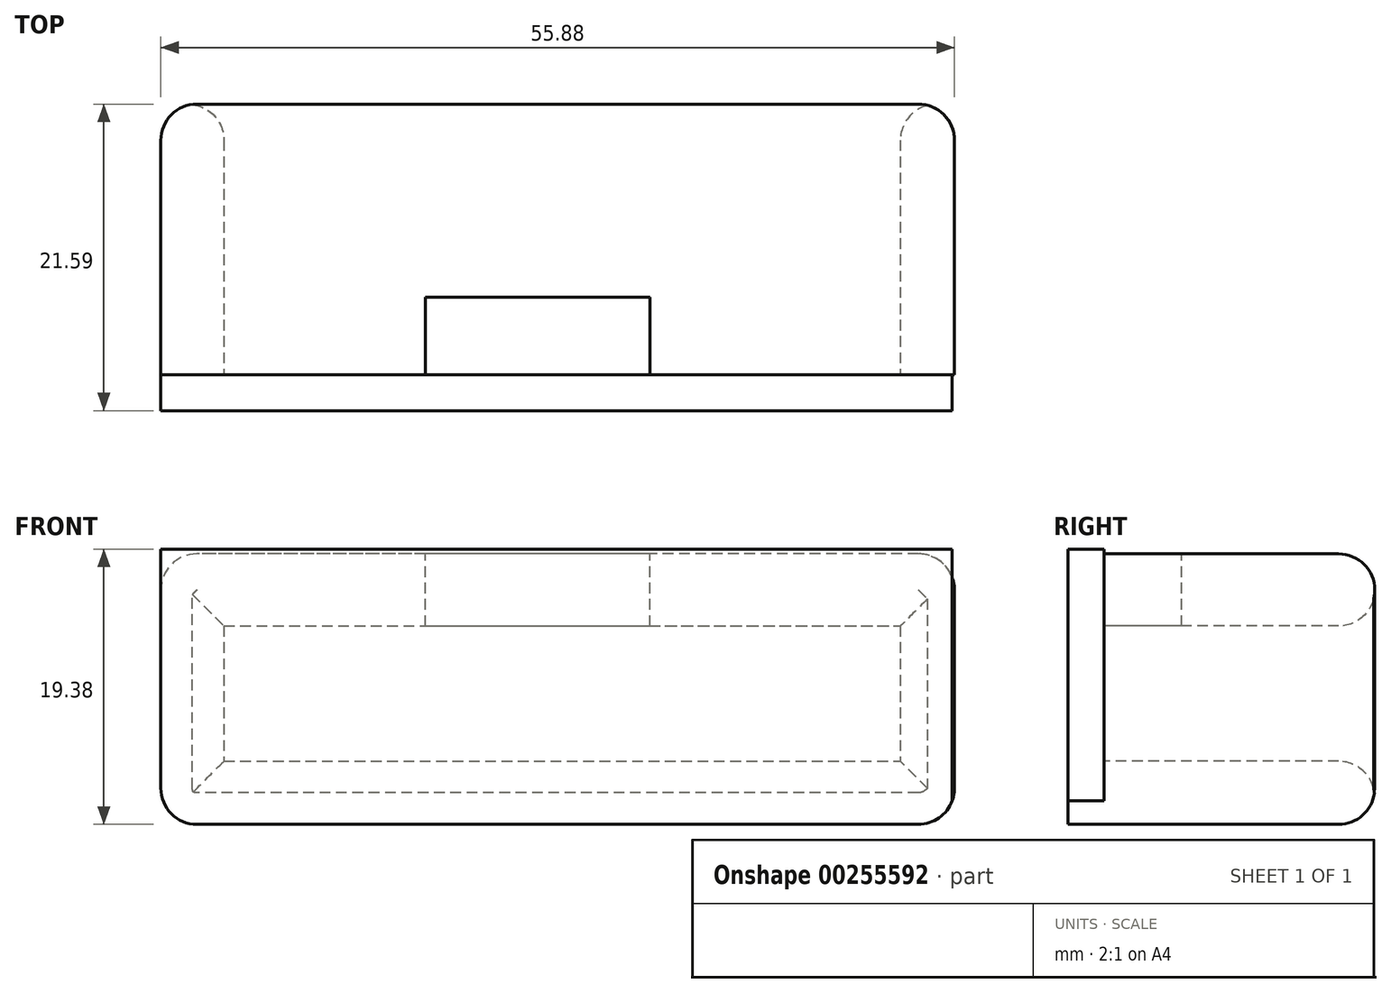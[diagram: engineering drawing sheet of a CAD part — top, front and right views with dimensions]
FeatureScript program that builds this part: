
annotation { "Feature Type Name" : "Feature", "Feature Type Description" : "" }
export const myFeature = defineFeature(function(context is Context, id is Id, definition is map)
    precondition{}
    {
        {
            var Q0;
            Q0=qCreatedBy(makeId("Right.planeOp"),FACE);
            var sketch = newSketch(context, id + "F0", { "sketchPlane" : qUnion([Q0])});
            skLineSegment(sketch, "E0.bottom", {"start": v(0, 0) * mm, "end": v(19.05, 0) * mm});
            skLineSegment(sketch, "E0.top", {"start": v(0, 19.05) * mm, "end": v(19.05, 19.05) * mm});
            skLineSegment(sketch, "E0.left", {"start": v(0, 0) * mm, "end": v(0, 19.05) * mm});
            skLineSegment(sketch, "E0.right", {"start": v(19.05, 0) * mm, "end": v(19.05, 19.05) * mm});
            skSolve(sketch);
        }
        {
            var Q0;
            Q0 = qSketchRegion(id + "F0", true);
            extrude(context, id + "F1", {"entities" : qUnion([Q0]), "depth" : 55.88 * mm});
        }
        {
            var Q0;
            Q0=makeQuery(id+"F1.opExtrude","SWEPT_FACE",FACE,{"disambiguationData":[OSD([sQuery(id+"F0.wireOp",EDGE,"E0.left")])]});
            var sketch = newSketch(context, id + "F2", { "sketchPlane" : qUnion([Q0])});
            skLineSegment(sketch, "E1.bottom", {"start": v(4.45, 13.97) * mm, "end": v(52.07, 13.97) * mm});
            skLineSegment(sketch, "E1.top", {"start": v(4.45, 4.44) * mm, "end": v(52.07, 4.44) * mm});
            skLineSegment(sketch, "E1.left", {"start": v(4.45, 13.97) * mm, "end": v(4.45, 4.44) * mm});
            skLineSegment(sketch, "E1.right", {"start": v(52.07, 13.97) * mm, "end": v(52.07, 4.44) * mm});
            skSolve(sketch);
        }
        {
            var Q0;
            Q0 = qSketchRegion(id + "F2", true);
            extrude(context, id + "F3", {"entities" : qUnion([Q0]), "operationType" : NewBodyOperationType.REMOVE, "oppositeDirection" : true, "depth" : 25.4 * mm});
        }
        {
            var Q0;
            Q0=qCreatedBy(makeId("Front.planeOp"),FACE);
            var sketch = newSketch(context, id + "F4", { "sketchPlane" : qUnion([Q0])});
            skLineSegment(sketch, "E2.bottom", {"start": v(0, 0) * mm, "end": v(55.73, 0) * mm});
            skLineSegment(sketch, "E2.top", {"start": v(0, 19.38) * mm, "end": v(55.73, 19.38) * mm});
            skLineSegment(sketch, "E2.left", {"start": v(0, 0) * mm, "end": v(0, 19.38) * mm});
            skLineSegment(sketch, "E2.right", {"start": v(55.73, 0) * mm, "end": v(55.73, 19.38) * mm});
            skSolve(sketch);
        }
        {
            var Q0;
            Q0 = qSketchRegion(id + "F4", true);
            extrude(context, id + "F5", {"entities" : qUnion([Q0]), "operationType" : NewBodyOperationType.ADD, "depth" : 2.54 * mm});
        }
        {
            var Q0;
            Q0=makeQuery(id+"F1.opExtrude","SWEPT_FACE",FACE,{"disambiguationData":[OSD([sQuery(id+"F0.wireOp",EDGE,"E0.right")])]});
            var Q1;
            Q1=makeQuery(id+"F1.opExtrude","CAP_EDGE",EDGE,{"disambiguationData":[OSD([sQuery(id+"F0.wireOp",EDGE,"E0.top")])],"isStart":true});
            var Q2;
            Q2=makeQuery(id+"F5.boolean.opBoolean","MERGE",EDGE,{"derivedFrom":[makeQuery(id+"F1.opExtrude","CAP_EDGE",EDGE,{"disambiguationData":[OSD([sQuery(id+"F0.wireOp",EDGE,"E0.bottom")])],"isStart":true}),makeQuery(id+"F5.opExtrude","SWEPT_EDGE",EDGE,{"disambiguationData":[OSD([sQuery(id+"F4.wireOp",EDGE,"E2.bottom"),sQuery(id+"F4.wireOp",EDGE,"E2.left")])]})]});
            var Q3;
            Q3=makeQuery(id+"F1.opExtrude","CAP_EDGE",EDGE,{"disambiguationData":[OSD([sQuery(id+"F0.wireOp",EDGE,"E0.top")])],"isStart":false});
            var Q4;
            Q4=makeQuery(id+"F1.opExtrude","CAP_EDGE",EDGE,{"disambiguationData":[OSD([sQuery(id+"F0.wireOp",EDGE,"E0.bottom")])],"isStart":false});
            fillet(context, id + "F6", {"entities" : qUnion([Q0, Q1, Q2, Q3, Q4]), "radius" : 2.54 * mm, "tangentPropagation" : true, "allowEdgeOverflow" : false});
        }
        {
            var Q0;
            Q0=makeQuery(id+"F1.opExtrude","SWEPT_FACE",FACE,{"disambiguationData":[OSD([sQuery(id+"F0.wireOp",EDGE,"E0.top")])]});
            var sketch = newSketch(context, id + "F7", { "sketchPlane" : qUnion([Q0])});
            skLineSegment(sketch, "E3.bottom", {"start": v(34.43, 0) * mm, "end": v(18.62, 0) * mm});
            skLineSegment(sketch, "E3.top", {"start": v(34.43, 5.46) * mm, "end": v(18.62, 5.46) * mm});
            skLineSegment(sketch, "E3.left", {"start": v(34.43, 0) * mm, "end": v(34.43, 5.46) * mm});
            skLineSegment(sketch, "E3.right", {"start": v(18.62, 0) * mm, "end": v(18.62, 5.46) * mm});
            skSolve(sketch);
        }
        {
            var Q0;
            Q0 = qSketchRegion(id + "F7", true);
            extrude(context, id + "F8", {"entities" : qUnion([Q0]), "operationType" : NewBodyOperationType.REMOVE, "oppositeDirection" : true, "depth" : 12.7 * mm});
        }
    });
